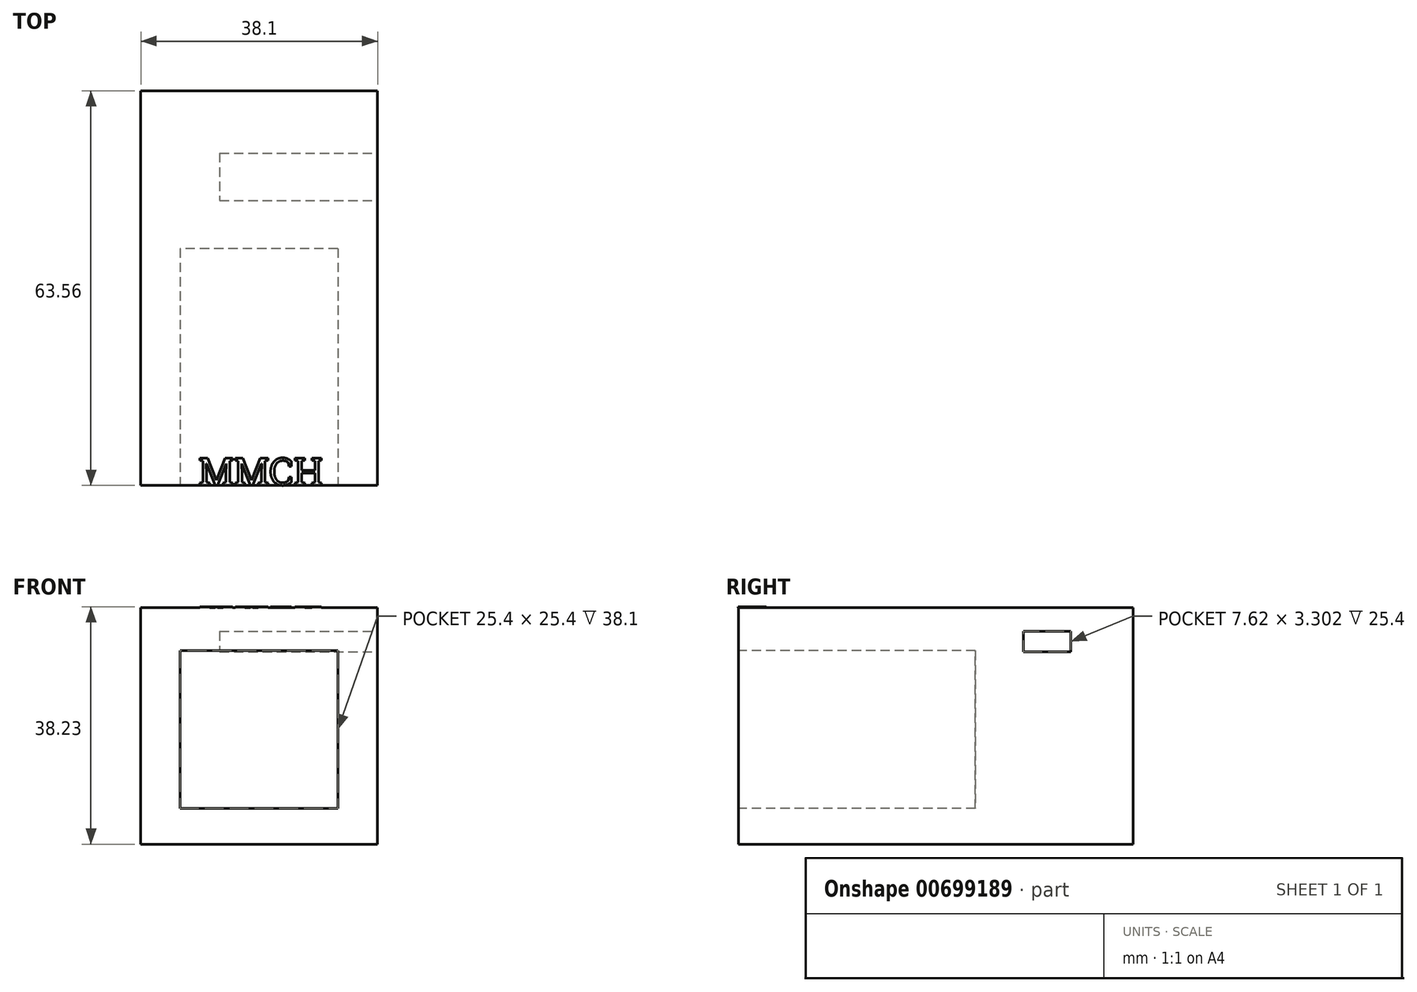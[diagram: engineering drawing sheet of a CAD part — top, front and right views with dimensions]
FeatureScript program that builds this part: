
annotation { "Feature Type Name" : "Feature", "Feature Type Description" : "" }
export const myFeature = defineFeature(function(context is Context, id is Id, definition is map)
    precondition{}
    {
        {
            var Q0;
            Q0=qCreatedBy(makeId("Front.planeOp"),FACE);
            var sketch = newSketch(context, id + "F0", { "sketchPlane" : qUnion([Q0])});
            skLineSegment(sketch, "E0", {"start": v(-39.81, 57.1) * mm, "end": v(-39.81, 19) * mm});
            skLineSegment(sketch, "E1", {"start": v(-39.81, 19) * mm, "end": v(-1.71, 19) * mm});
            skLineSegment(sketch, "E2", {"start": v(-1.71, 19) * mm, "end": v(-1.71, 57.1) * mm});
            skLineSegment(sketch, "E3", {"start": v(-1.71, 57.1) * mm, "end": v(-39.81, 57.1) * mm});
            skSolve(sketch);
        }
        {
            var Q0;
            Q0 = qSketchRegion(id + "F0", true);
            extrude(context, id + "F1", {"entities" : qUnion([Q0]), "depth" : 63.5 * mm, "offsetDistance" : 25.4 * mm});
        }
        {
            var Q0;
            Q0=makeQuery(id+"F1.opExtrude","CAP_FACE",FACE,{"disambiguationData":[OSD([sQuery(id+"F0.wireOp",EDGE,"E0"),sQuery(id+"F0.wireOp",EDGE,"E1"),sQuery(id+"F0.wireOp",EDGE,"E2"),sQuery(id+"F0.wireOp",EDGE,"E3")])],"isStart":false});
            var sketch = newSketch(context, id + "F2", { "sketchPlane" : qUnion([Q0])});
            skLineSegment(sketch, "E4", {"start": v(-33.51, 50.13) * mm, "end": v(-33.51, 24.73) * mm});
            skLineSegment(sketch, "E5", {"start": v(-33.51, 24.73) * mm, "end": v(-8.11, 24.73) * mm});
            skLineSegment(sketch, "E6", {"start": v(-8.11, 24.73) * mm, "end": v(-8.11, 50.13) * mm});
            skLineSegment(sketch, "E7", {"start": v(-8.11, 50.13) * mm, "end": v(-33.51, 50.13) * mm});
            skSolve(sketch);
        }
        {
            var Q0;
            Q0 = qSketchRegion(id + "F2", true);
            extrude(context, id + "F3", {"entities" : qUnion([Q0]), "operationType" : NewBodyOperationType.REMOVE, "oppositeDirection" : true, "depth" : 38.1 * mm, "offsetDistance" : 25.4 * mm});
        }
        {
            var Q0;
            Q0=makeQuery(id+"F1.opExtrude","SWEPT_FACE",FACE,{"disambiguationData":[OSD([sQuery(id+"F0.wireOp",EDGE,"E2")])]});
            var sketch = newSketch(context, id + "F4", { "sketchPlane" : qUnion([Q0])});
            skLineSegment(sketch, "E8", {"start": v(-17.66, 53.24) * mm, "end": v(-17.66, 49.93) * mm});
            skLineSegment(sketch, "E9", {"start": v(-17.66, 49.93) * mm, "end": v(-10.04, 49.93) * mm});
            skLineSegment(sketch, "E10", {"start": v(-10.04, 49.93) * mm, "end": v(-10.04, 53.24) * mm});
            skLineSegment(sketch, "E11", {"start": v(-10.04, 53.24) * mm, "end": v(-17.66, 53.24) * mm});
            skSolve(sketch);
        }
        {
            var Q0;
            Q0 = qSketchRegion(id + "F4", true);
            extrude(context, id + "F5", {"entities" : qUnion([Q0]), "operationType" : NewBodyOperationType.REMOVE, "oppositeDirection" : true, "depth" : 25.4 * mm, "offsetDistance" : 25.4 * mm});
        }
        {
            var Q0;
            Q0=makeQuery(id+"F1.opExtrude","SWEPT_FACE",FACE,{"disambiguationData":[OSD([sQuery(id+"F0.wireOp",EDGE,"E3")])]});
            var sketch = newSketch(context, id + "F6", { "sketchPlane" : qUnion([Q0])});
            skText(sketch, "E12", { "text": "MMCH", "fontName": "RobotoSlab-Regular.ttf"});
            const initialGuessF6  = {"E12": [-0.03051, -0.0635, 1, 0, 0.0044]};
            skSetInitialGuess(sketch, initialGuessF6);
            skSolve(sketch);
        }
        {
            var Q0;
            Q0 = qSketchRegion(id + "F6", true);
            extrude(context, id + "F7", {"entities" : qUnion([Q0]), "operationType" : NewBodyOperationType.ADD, "depth" : 0.13 * mm, "offsetDistance" : 25.4 * mm});
        }
    });
